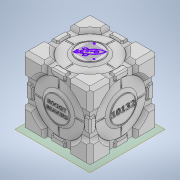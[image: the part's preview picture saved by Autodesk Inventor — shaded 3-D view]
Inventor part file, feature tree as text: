
AUTODESK INVENTOR PART (.ipt)
format: ipt  version: 2020 (Build 240168000, 168)  size: 2,704,896 bytes
history: native  units: in
note: dims shown in document units (in); Inventor stores cm internally (conversion verified against a paired STEP export)
features: other x10, sketch x7, chamfer x4, emboss x4, extrude x3, fillet x2, boolean_combine x1, plane x1
ambient origin geometry x8: Origin, YZ Plane, XZ Plane, XY Plane, X Axis, Y Axis, Z Axis, Center Point
bodies: Solid1 (feature_tree), Solid2 (feature_tree), Solid3 (feature_tree), Solid4 (feature_tree), Solid5 (feature_tree), Solid6 (feature_tree), Solid7 (feature_tree), Solid8 (feature_tree)
feature tree (32):
  other  "Portal Companion Cube.iam"
  other  "Portal Companion Cube.ipt:1"
  other  "Portal Companion Cube.ipt:2"
  other  "Portal Companion Cube.ipt:3"
  other  "Portal Companion Cube.ipt:4"
  other  "Portal Companion Cube_MIR.ipt:1"
  other  "Portal Companion Cube_MIR.ipt:2"
  other  "Portal Companion Cube_MIR.ipt:3"
  other  "Portal Companion Cube_MIR.ipt:4"
  boolean_combine  "Combine1"
  plane  "Work Plane1"
  extrude  "Extrusion1"  Depth=0.175in
  extrude  "Extrusion2"  Depth=0.175in
  extrude  "Extrusion3"  Depth=0.3in TaperAngle=0.0deg
  chamfer  "Chamfer1"  Distance=0.05in
  chamfer  "Chamfer2"  Distance=0.0375in
  chamfer  "Chamfer3"  Distance=0.25in
  chamfer  "Chamfer4"  Distance=0.0375in Angle=45.0deg
  fillet  "Fillet1"  Radius=0.0375in
  fillet  "Fillet2"  Radius=0.0375in
  sketch  "Sketch4"  dims[d7=0.74in d8=0.05in d9=0.0in]
  sketch  "Sketch5"  dims[d10=0.0375in]
  sketch  "Sketch6"  dims[d11=0.0375in]
  emboss  "Emboss1"
  emboss  "Emboss2"
  emboss  "Emboss3"
  emboss  "Emboss4"
  sketch  "Sketch1"  dims[d0=0.3937in d1=0.175in]
  sketch  "Sketch2"  dims[d2=0.175in d3=0.175in]
  sketch  "Sketch3"  dims[d4=0.175in d5=0.3in d6=0.0in]
  sketch  "Sketch7"  dims[d12=0.0375in d13=0.0375in d14=0.25in d15=0.0in d16=0.0375in d17=0.25in d18=45.0deg d19=0.0375in d20=0.25in d21=45.0deg d22=0.0375in d23=0.25in d24=45.0deg d25=0.0375in d26=0.25in d27=45.0deg d28=0.02in d29=0.02in d30=0.05in d31=0.0in d32=0.05in d33=0.0in d34=0.05in d35=0.0in d36=0.05in d37=0.0in]
  other  "Image1"
